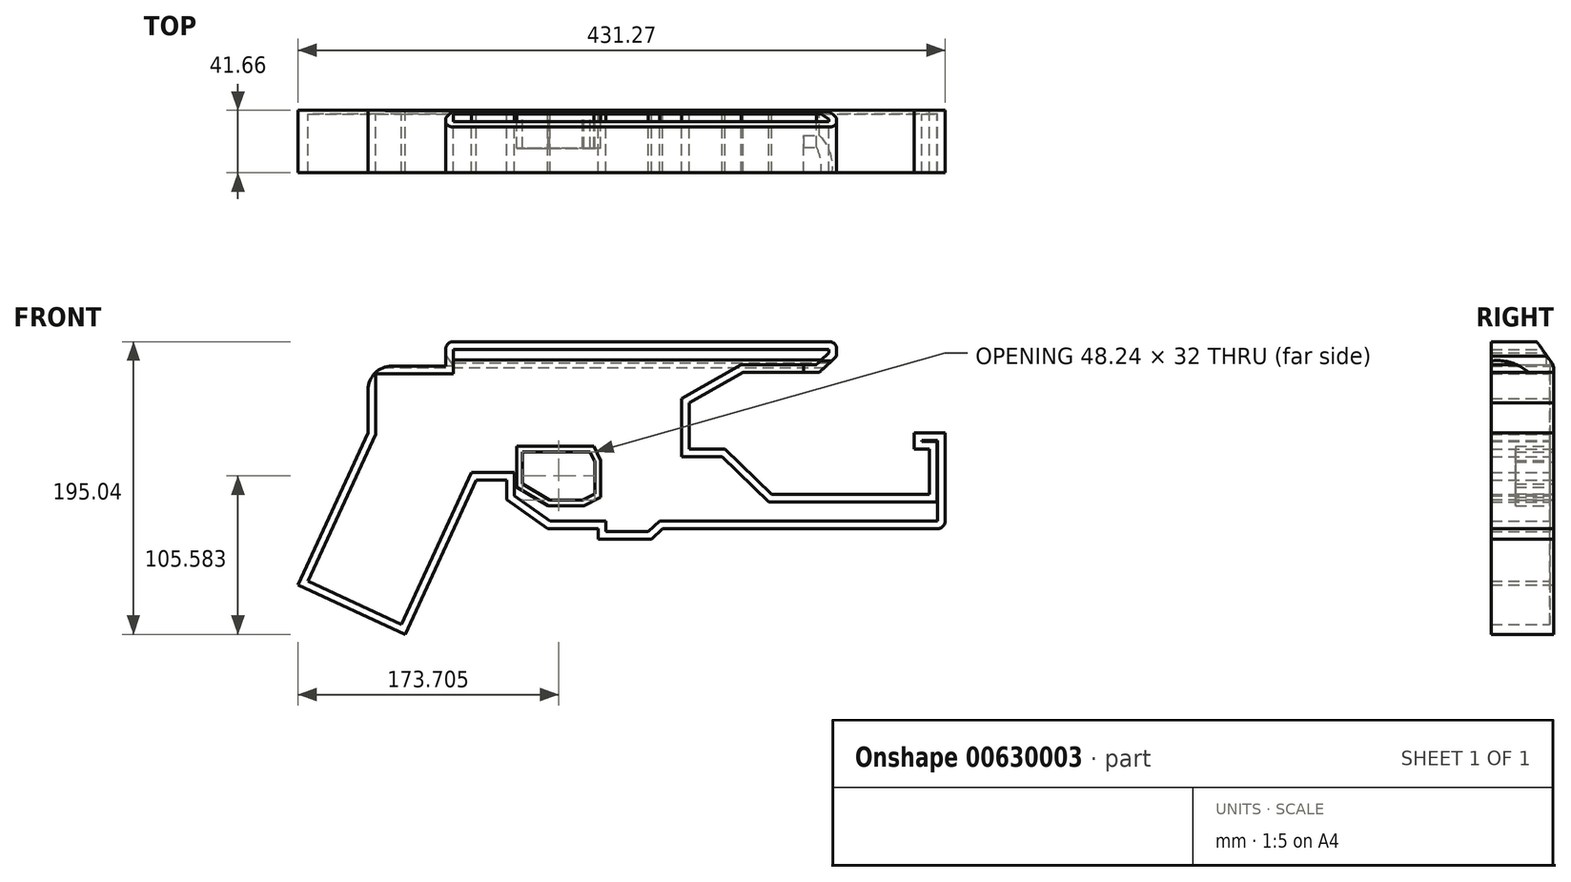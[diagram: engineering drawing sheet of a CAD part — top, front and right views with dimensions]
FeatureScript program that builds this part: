
annotation { "Feature Type Name" : "Feature", "Feature Type Description" : "" }
export const myFeature = defineFeature(function(context is Context, id is Id, definition is map)
    precondition{}
    {
        {
            var Q0;
            Q0=qCreatedBy(makeId("Front.planeOp"),FACE);
            var sketch = newSketch(context, id + "F0", { "sketchPlane" : qUnion([Q0])});
            skLineSegment(sketch, "E0", {"start": v(138.67, 60.77) * mm, "end": v(-121.84, 60.77) * mm});
            skLineSegment(sketch, "E1", {"start": v(-121.84, 60.77) * mm, "end": v(-121.84, 44.56) * mm});
            skLineSegment(sketch, "E2", {"start": v(-121.84, 44.56) * mm, "end": v(-173.57, 44.56) * mm});
            skLineSegment(sketch, "E3", {"start": v(-173.57, 44.56) * mm, "end": v(-173.57, 0) * mm});
            skLineSegment(sketch, "E4", {"start": v(-173.57, 0) * mm, "end": v(-220.31, -101.28) * mm});
            skLineSegment(sketch, "E5", {"start": v(-220.31, -101.28) * mm, "end": v(-148.82, -134.27) * mm});
            skLineSegment(sketch, "E6", {"start": v(-148.82, -134.27) * mm, "end": v(-101.43, -31.6) * mm});
            skLineSegment(sketch, "E7", {"start": v(-101.43, -31.6) * mm, "end": v(-81.33, -31.6) * mm});
            skLineSegment(sketch, "E8", {"start": v(-81.33, -31.6) * mm, "end": v(-81.33, -44.56) * mm});
            skLineSegment(sketch, "E9", {"start": v(-81.33, -44.56) * mm, "end": v(-53.9, -63.88) * mm});
            skLineSegment(sketch, "E10", {"start": v(-53.9, -63.88) * mm, "end": v(-20.26, -63.88) * mm});
            skLineSegment(sketch, "E11", {"start": v(-20.26, -63.88) * mm, "end": v(-20.26, -70.74) * mm});
            skLineSegment(sketch, "E12", {"start": v(-20.26, -70.74) * mm, "end": v(15.27, -70.74) * mm});
            skLineSegment(sketch, "E13", {"start": v(15.27, -70.74) * mm, "end": v(22.75, -63.88) * mm});
            skLineSegment(sketch, "E14", {"start": v(22.75, -63.88) * mm, "end": v(210.96, -63.88) * mm});
            skLineSegment(sketch, "E15", {"start": v(210.96, -63.88) * mm, "end": v(210.96, 0) * mm});
            skLineSegment(sketch, "E16", {"start": v(210.96, 0) * mm, "end": v(190.4, 0) * mm});
            skLineSegment(sketch, "E17", {"start": v(190.4, 0) * mm, "end": v(190.4, -10.9) * mm});
            skLineSegment(sketch, "E18", {"start": v(190.4, -10.9) * mm, "end": v(200.46, -10.9) * mm});
            skLineSegment(sketch, "E19", {"start": v(200.46, -10.9) * mm, "end": v(200.46, -41.05) * mm});
            skLineSegment(sketch, "E20", {"start": v(200.46, -41.05) * mm, "end": v(95.45, -41.05) * mm});
            skLineSegment(sketch, "E21", {"start": v(95.45, -41.05) * mm, "end": v(64.3, -10.9) * mm});
            skLineSegment(sketch, "E22", {"start": v(64.3, -10.9) * mm, "end": v(40.39, -10.9) * mm});
            skLineSegment(sketch, "E23", {"start": v(40.39, -10.9) * mm, "end": v(40.39, 20.03) * mm});
            skLineSegment(sketch, "E24", {"start": v(40.39, 20.03) * mm, "end": v(76.27, 40.36) * mm});
            skLineSegment(sketch, "E25", {"start": v(76.27, 40.36) * mm, "end": v(127.1, 40.36) * mm});
            skLineSegment(sketch, "E26", {"start": v(-70.72, -12.7) * mm, "end": v(-70.72, -34.03) * mm});
            skLineSegment(sketch, "E27", {"start": v(-70.72, -34.03) * mm, "end": v(-52.45, -44.69) * mm});
            skLineSegment(sketch, "E28", {"start": v(-52.45, -44.69) * mm, "end": v(-30.61, -44.69) * mm});
            skLineSegment(sketch, "E29", {"start": v(-30.61, -44.69) * mm, "end": v(-22.49, -40.62) * mm});
            skLineSegment(sketch, "E30", {"start": v(-22.49, -40.62) * mm, "end": v(-22.49, -19.29) * mm});
            skLineSegment(sketch, "E31", {"start": v(-22.49, -19.29) * mm, "end": v(-25.52, -12.69) * mm});
            skLineSegment(sketch, "E32", {"start": v(-25.52, -12.69) * mm, "end": v(-70.72, -12.7) * mm});
            skLineSegment(sketch, "E33", {"start": v(138.67, 60.77) * mm, "end": v(138.67, 51.02) * mm});
            skLineSegment(sketch, "E34", {"start": v(138.67, 51.02) * mm, "end": v(127.1, 40.36) * mm});
            skLineSegment(sketch, "E35.0", {"start": v(-168.5, 39.48) * mm, "end": v(-168.5, -1.12) * mm});
            skLineSegment(sketch, "E35.1", {"start": v(-116.76, 39.48) * mm, "end": v(-168.5, 39.48) * mm});
            skLineSegment(sketch, "E35.2", {"start": v(-116.76, 55.69) * mm, "end": v(-116.76, 39.48) * mm});
            skLineSegment(sketch, "E35.3", {"start": v(133.59, 55.69) * mm, "end": v(-116.76, 55.69) * mm});
            skLineSegment(sketch, "E35.4", {"start": v(133.59, 55.69) * mm, "end": v(133.59, 53.25) * mm});
            skLineSegment(sketch, "E35.5", {"start": v(20.77, -58.8) * mm, "end": v(205.88, -58.8) * mm});
            skLineSegment(sketch, "E35.6", {"start": v(13.3, -65.66) * mm, "end": v(20.77, -58.8) * mm});
            skLineSegment(sketch, "E35.7", {"start": v(-15.18, -65.66) * mm, "end": v(13.3, -65.66) * mm});
            skLineSegment(sketch, "E35.8", {"start": v(-15.18, -58.8) * mm, "end": v(-15.18, -65.66) * mm});
            skLineSegment(sketch, "E35.9", {"start": v(-52.3, -58.8) * mm, "end": v(-15.18, -58.8) * mm});
            skLineSegment(sketch, "E35.10", {"start": v(-76.25, -41.93) * mm, "end": v(-52.3, -58.8) * mm});
            skLineSegment(sketch, "E35.11", {"start": v(-213.57, -98.8) * mm, "end": v(-151.3, -127.53) * mm});
            skLineSegment(sketch, "E35.12", {"start": v(-151.3, -127.53) * mm, "end": v(-104.68, -26.51) * mm});
            skLineSegment(sketch, "E35.13", {"start": v(-104.68, -26.51) * mm, "end": v(-76.25, -26.51) * mm});
            skLineSegment(sketch, "E35.14", {"start": v(-76.25, -26.51) * mm, "end": v(-76.25, -41.93) * mm});
            skLineSegment(sketch, "E35.15", {"start": v(205.88, -58.8) * mm, "end": v(205.88, -5.08) * mm});
            skLineSegment(sketch, "E35.16", {"start": v(205.88, -5.08) * mm, "end": v(195.48, -5.08) * mm});
            skLineSegment(sketch, "E35.17", {"start": v(195.48, -5.08) * mm, "end": v(195.48, -5.83) * mm});
            skLineSegment(sketch, "E35.18", {"start": v(195.48, -5.83) * mm, "end": v(205.54, -5.83) * mm});
            skLineSegment(sketch, "E35.19", {"start": v(205.54, -5.83) * mm, "end": v(205.54, -46.13) * mm});
            skLineSegment(sketch, "E35.20", {"start": v(-168.5, -1.12) * mm, "end": v(-213.57, -98.8) * mm});
            skLineSegment(sketch, "E35.21", {"start": v(205.54, -46.13) * mm, "end": v(93.4, -46.13) * mm});
            skLineSegment(sketch, "E35.22", {"start": v(93.4, -46.13) * mm, "end": v(62.24, -15.99) * mm});
            skLineSegment(sketch, "E35.23", {"start": v(62.24, -15.99) * mm, "end": v(35.3, -15.99) * mm});
            skLineSegment(sketch, "E35.24", {"start": v(35.3, -15.99) * mm, "end": v(35.3, 22.99) * mm});
            skLineSegment(sketch, "E35.25", {"start": v(35.3, 22.99) * mm, "end": v(74.94, 45.44) * mm});
            skLineSegment(sketch, "E35.26", {"start": v(74.94, 45.44) * mm, "end": v(125.11, 45.44) * mm});
            skLineSegment(sketch, "E35.27", {"start": v(133.59, 53.25) * mm, "end": v(125.11, 45.44) * mm});
            skLineSegment(sketch, "E36.0", {"start": v(-18.68, -18.45) * mm, "end": v(-23.08, -8.87) * mm});
            skLineSegment(sketch, "E36.1", {"start": v(-18.68, -42.97) * mm, "end": v(-18.68, -18.45) * mm});
            skLineSegment(sketch, "E36.2", {"start": v(-74.53, -8.9) * mm, "end": v(-74.53, -36.22) * mm});
            skLineSegment(sketch, "E36.3", {"start": v(-74.53, -36.22) * mm, "end": v(-53.48, -48.5) * mm});
            skLineSegment(sketch, "E36.4", {"start": v(-53.48, -48.5) * mm, "end": v(-29.71, -48.5) * mm});
            skLineSegment(sketch, "E36.5", {"start": v(-23.08, -8.87) * mm, "end": v(-74.53, -8.9) * mm});
            skLineSegment(sketch, "E36.6", {"start": v(-29.71, -48.5) * mm, "end": v(-18.68, -42.97) * mm});
            skSolve(sketch);
        }
        {
            var Q0;
            Q0=makeQuery(id+"F0.imprint","IMPRINT",FACE,{"disambiguationData":[TD([[makeQuery(id+"F0.imprint","IMPRINT",EDGE,{"derivedFrom":sQuery(id+"F0.wireOp",EDGE,"E0")}),1.0]])]});
            extrude(context, id + "F1", {"entities" : qUnion([Q0]), "depth" : 41.66 * mm, "offsetDistance" : 25.4 * mm});
        }
        {
            var Q0;
            Q0=makeQuery(id+"F1.opExtrude","SWEPT_EDGE",EDGE,{"disambiguationData":[OSD([sQuery(id+"F0.wireOp",EDGE,"E2"),sQuery(id+"F0.wireOp",EDGE,"E3")])]});
            fillet(context, id + "F2", {"entities" : qUnion([Q0]), "radius" : 15.94 * mm, "tangentPropagation" : true, "allowEdgeOverflow" : false});
        }
        {
            var Q0;
            Q0=makeQuery(id+"F1.opExtrude","SWEPT_EDGE",EDGE,{"disambiguationData":[OSD([sQuery(id+"F0.wireOp",EDGE,"E0"),sQuery(id+"F0.wireOp",EDGE,"E1")])]});
            var Q1;
            Q1=makeQuery(id+"F1.opExtrude","SWEPT_EDGE",EDGE,{"disambiguationData":[OSD([sQuery(id+"F0.wireOp",EDGE,"E14"),sQuery(id+"F0.wireOp",EDGE,"E15")])]});
            var Q2;
            Q2=makeQuery(id+"F1.opExtrude","SWEPT_EDGE",EDGE,{"disambiguationData":[OSD([sQuery(id+"F0.wireOp",EDGE,"E0"),sQuery(id+"F0.wireOp",EDGE,"E33")])]});
            fillet(context, id + "F3", {"entities" : qUnion([Q0, Q1, Q2]), "radius" : 5.08 * mm, "tangentPropagation" : true, "allowEdgeOverflow" : false});
        }
        {
            var Q0;
            Q0=makeQuery(id+"F0.imprint","IMPRINT",FACE,{"disambiguationData":[TD([[makeQuery(id+"F0.imprint","IMPRINT",EDGE,{"derivedFrom":sQuery(id+"F0.wireOp",EDGE,"E35.0")}),1.0]])]});
            extrude(context, id + "F4", {"entities" : qUnion([Q0]), "operationType" : NewBodyOperationType.ADD, "depth" : 2.54 * mm, "offsetDistance" : 25.4 * mm});
        }
        {
            var Q0;
            Q0=makeQuery(id+"F0.imprint","IMPRINT",FACE,{"disambiguationData":[TD([[makeQuery(id+"F0.imprint","IMPRINT",EDGE,{"derivedFrom":sQuery(id+"F0.wireOp",EDGE,"E26")}),-1.0]])]});
            extrude(context, id + "F5", {"entities" : qUnion([Q0]), "operationType" : NewBodyOperationType.ADD, "depth" : 25.4 * mm, "offsetDistance" : 25.4 * mm});
        }
        {
            var Q0;
            Q0=makeQuery(id+"F1.opExtrude","CAP_EDGE",EDGE,{"disambiguationData":[OSD([sQuery(id+"F0.wireOp",EDGE,"E0")])],"isStart":true});
            chamfer(context, id + "F6", {"entities" : qUnion([Q0]), "width" : 5.08 * mm, "tangentPropagation" : true});
        }
        {
            var Q0;
            Q0=qCreatedBy(makeId("Right.planeOp"),FACE);
            cPlane(context, id + "F7", {"entities" : qUnion([Q0]), "cplaneType" : CPlaneType.OFFSET, "offset" : 152.65 * mm, "width" : 152.4 * mm, "height" : 152.4 * mm});
        }
        {
            var Q0;
            Q0=qCreatedBy(id+"F7.planeOp",FACE);
            var sketch = newSketch(context, id + "F8", { "sketchPlane" : qUnion([Q0])});
            skArc(sketch, "E37", {"start": v(-15.86, 39.6) * mm, "mid": v(-28.9, 46.96) * mm, "end": v(-43.87, 47.6) * mm});
            skLineSegment(sketch, "E38", {"start": v(-43.87, 47.6) * mm, "end": v(-37.73, 16.07) * mm});
            skLineSegment(sketch, "E39", {"start": v(-15.86, 39.6) * mm, "end": v(-37.73, 16.07) * mm});
            skSolve(sketch);
        }
        {
            var Q0;
            Q0=makeQuery(id+"F8.imprint","IMPRINT",FACE,{"disambiguationData":[TD([[makeQuery(id+"F8.imprint","IMPRINT",EDGE,{"derivedFrom":sQuery(id+"F8.wireOp",EDGE,"E37")}),1.0]])]});
            extrude(context, id + "F9", {"entities" : qUnion([Q0]), "operationType" : NewBodyOperationType.REMOVE, "oppositeDirection" : true, "depth" : 36.07 * mm, "offsetDistance" : 25.4 * mm});
        }
        {
            var Q0;
            Q0=qCreatedBy(makeId("Right.planeOp"),FACE);
            var sketch = newSketch(context, id + "F10", { "sketchPlane" : qUnion([Q0])});
            skLineSegment(sketch, "E40", {"start": v(7.07, 34.96) * mm, "end": v(-20.42, 73.76) * mm});
            skLineSegment(sketch, "E41", {"start": v(-20.42, 73.76) * mm, "end": v(19.2, 65.28) * mm});
            skLineSegment(sketch, "E42", {"start": v(19.2, 65.28) * mm, "end": v(7.07, 34.96) * mm});
            skSolve(sketch);
        }
        {
            var Q0;
            Q0=makeQuery(id+"F10.imprint","IMPRINT",FACE,{"disambiguationData":[TD([[makeQuery(id+"F10.imprint","IMPRINT",EDGE,{"derivedFrom":sQuery(id+"F10.wireOp",EDGE,"E40")}),-1.0]])]});
            extrude(context, id + "F11", {"entities" : qUnion([Q0]), "operationType" : NewBodyOperationType.REMOVE, "endBound" : BoundingType.SYMMETRIC, "oppositeDirection" : true, "depth" : 407.92 * mm, "offsetDistance" : 25.4 * mm});
        }
        {
            var Q0;
            {var subQ0=sQuery(id+"F0.wireOp",EDGE,"E36.6");var subQ1=sQuery(id+"F0.wireOp",EDGE,"E36.5");var subQ2=sQuery(id+"F0.wireOp",EDGE,"E36.4");var subQ3=sQuery(id+"F0.wireOp",EDGE,"E36.3");var subQ4=sQuery(id+"F0.wireOp",EDGE,"E36.2");var subQ5=sQuery(id+"F0.wireOp",EDGE,"E36.1");var subQ6=sQuery(id+"F0.wireOp",EDGE,"E36.0");var subQ7=sQuery(id+"F0.wireOp",EDGE,"E35.27");var subQ8=sQuery(id+"F0.wireOp",EDGE,"E35.26");var subQ9=sQuery(id+"F0.wireOp",EDGE,"E35.25");var subQ10=sQuery(id+"F0.wireOp",EDGE,"E35.24");var subQ11=sQuery(id+"F0.wireOp",EDGE,"E35.23");var subQ12=sQuery(id+"F0.wireOp",EDGE,"E35.22");var subQ13=sQuery(id+"F0.wireOp",EDGE,"E35.21");var subQ14=sQuery(id+"F0.wireOp",EDGE,"E35.20");var subQ15=sQuery(id+"F0.wireOp",EDGE,"E35.19");var subQ16=sQuery(id+"F0.wireOp",EDGE,"E35.18");var subQ17=sQuery(id+"F0.wireOp",EDGE,"E35.17");var subQ18=sQuery(id+"F0.wireOp",EDGE,"E35.16");var subQ19=sQuery(id+"F0.wireOp",EDGE,"E35.15");var subQ20=sQuery(id+"F0.wireOp",EDGE,"E35.14");var subQ21=sQuery(id+"F0.wireOp",EDGE,"E35.13");var subQ22=sQuery(id+"F0.wireOp",EDGE,"E35.12");var subQ23=sQuery(id+"F0.wireOp",EDGE,"E35.11");var subQ24=sQuery(id+"F0.wireOp",EDGE,"E35.10");var subQ25=sQuery(id+"F0.wireOp",EDGE,"E35.9");var subQ26=sQuery(id+"F0.wireOp",EDGE,"E35.8");var subQ27=sQuery(id+"F0.wireOp",EDGE,"E35.7");var subQ28=sQuery(id+"F0.wireOp",EDGE,"E35.6");var subQ29=sQuery(id+"F0.wireOp",EDGE,"E35.5");var subQ30=sQuery(id+"F0.wireOp",EDGE,"E35.4");var subQ31=sQuery(id+"F0.wireOp",EDGE,"E35.3");var subQ32=sQuery(id+"F0.wireOp",EDGE,"E35.2");var subQ33=sQuery(id+"F0.wireOp",EDGE,"E35.1");var subQ34=sQuery(id+"F0.wireOp",EDGE,"E35.0");Q0=makeQuery(id+"F11.boolean.opBoolean","INTERSECT",EDGE,{"derivedFrom":[makeQuery(id+"F5.boolean.opBoolean","MERGE",FACE,{"derivedFrom":[makeQuery(id+"F4.boolean.opBoolean","MERGE",FACE,{"derivedFrom":[makeQuery(id+"F1.opExtrude","CAP_FACE",FACE,{"disambiguationData":[OSD([sQuery(id+"F0.wireOp",EDGE,"E0"),sQuery(id+"F0.wireOp",EDGE,"E1"),sQuery(id+"F0.wireOp",EDGE,"E2"),sQuery(id+"F0.wireOp",EDGE,"E3"),sQuery(id+"F0.wireOp",EDGE,"E4"),sQuery(id+"F0.wireOp",EDGE,"E5"),sQuery(id+"F0.wireOp",EDGE,"E6"),sQuery(id+"F0.wireOp",EDGE,"E7"),sQuery(id+"F0.wireOp",EDGE,"E8"),sQuery(id+"F0.wireOp",EDGE,"E9"),sQuery(id+"F0.wireOp",EDGE,"E10"),sQuery(id+"F0.wireOp",EDGE,"E11"),sQuery(id+"F0.wireOp",EDGE,"E12"),sQuery(id+"F0.wireOp",EDGE,"E13"),sQuery(id+"F0.wireOp",EDGE,"E14"),sQuery(id+"F0.wireOp",EDGE,"E15"),sQuery(id+"F0.wireOp",EDGE,"E16"),sQuery(id+"F0.wireOp",EDGE,"E17"),sQuery(id+"F0.wireOp",EDGE,"E18"),sQuery(id+"F0.wireOp",EDGE,"E19"),sQuery(id+"F0.wireOp",EDGE,"E20"),sQuery(id+"F0.wireOp",EDGE,"E21"),sQuery(id+"F0.wireOp",EDGE,"E22"),sQuery(id+"F0.wireOp",EDGE,"E23"),sQuery(id+"F0.wireOp",EDGE,"E24"),sQuery(id+"F0.wireOp",EDGE,"E25"),sQuery(id+"F0.wireOp",EDGE,"E33"),sQuery(id+"F0.wireOp",EDGE,"E34"),subQ34,subQ33,subQ32,subQ31,subQ30,subQ29,subQ28,subQ27,subQ26,subQ25,subQ24,subQ23,subQ22,subQ21,subQ20,subQ19,subQ18,subQ17,subQ16,subQ15,subQ14,subQ13,subQ12,subQ11,subQ10,subQ9,subQ8,subQ7])],"isStart":true}),makeQuery(id+"F4.opExtrude","CAP_FACE",FACE,{"disambiguationData":[OSD([subQ34,subQ33,subQ32,subQ31,subQ30,subQ29,subQ28,subQ27,subQ26,subQ25,subQ24,subQ23,subQ22,subQ21,subQ20,subQ19,subQ18,subQ17,subQ16,subQ15,subQ14,subQ13,subQ12,subQ11,subQ10,subQ9,subQ8,subQ7,subQ6,subQ5,subQ4,subQ3,subQ2,subQ1,subQ0])],"isStart":true})]}),makeQuery(id+"F5.opExtrude","CAP_FACE",FACE,{"disambiguationData":[OSD([sQuery(id+"F0.wireOp",EDGE,"E26"),sQuery(id+"F0.wireOp",EDGE,"E27"),sQuery(id+"F0.wireOp",EDGE,"E28"),sQuery(id+"F0.wireOp",EDGE,"E29"),sQuery(id+"F0.wireOp",EDGE,"E30"),sQuery(id+"F0.wireOp",EDGE,"E31"),sQuery(id+"F0.wireOp",EDGE,"E32"),subQ6,subQ5,subQ4,subQ3,subQ2,subQ1,subQ0])],"isStart":true})]}),makeQuery(id+"F11.opExtrude","SWEPT_FACE",FACE,{"disambiguationData":[OSD([sQuery(id+"F10.wireOp",EDGE,"E40")])]})]});}
            chamfer(context, id + "F12", {"entities" : qUnion([Q0]), "width" : 5.08 * mm, "tangentPropagation" : true});
        }
    });
